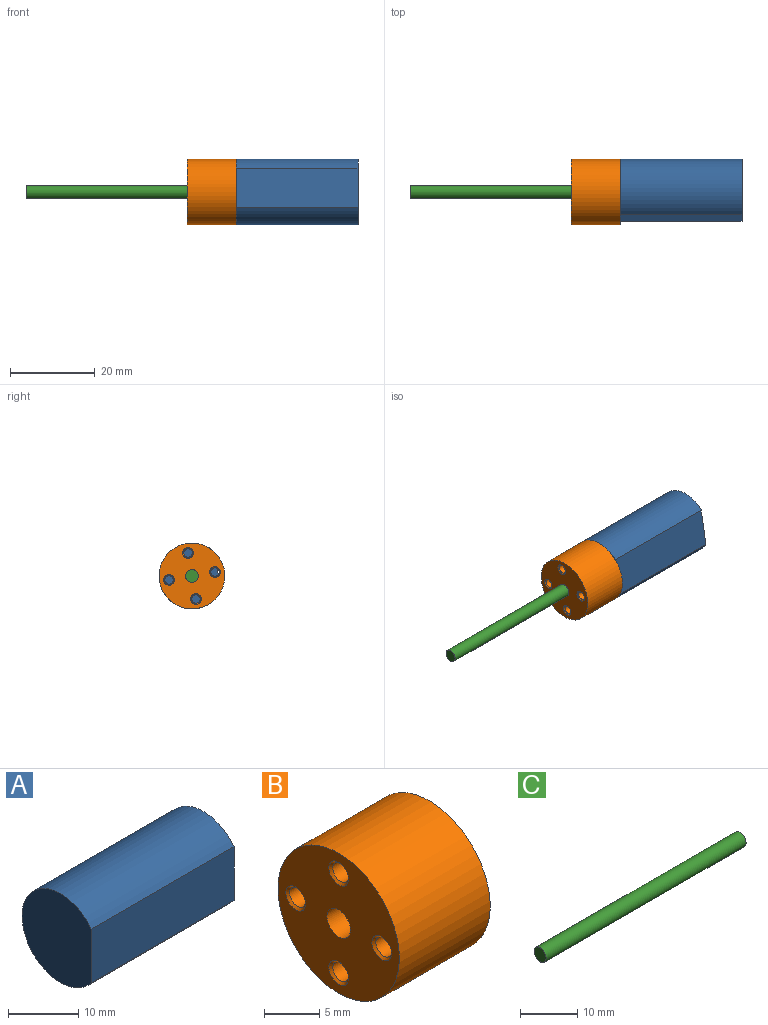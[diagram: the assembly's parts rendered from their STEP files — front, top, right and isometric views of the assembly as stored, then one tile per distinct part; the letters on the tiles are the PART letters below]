
ASSEMBLY  parts=3 mates=2
PART A: 4 faces, bbox 28.7x13.9x15.5 mm
  f0: cylinder r=7.75mm len=28.7mm, axis (-1,0,0), area 1109.8mm2, adj f1,f2,f3
  f1: plane 28.7x9.34mm, normal (0,-1,0), area 268.1mm2, adj f0,f2,f3
  f2: plane 15.5x13.93mm, normal (1,0,0), area 178.7mm2, adj f0,f1
  f3: plane 15.5x13.93mm, normal (-1,0,0), area 178.7mm2, adj f0,f1
PART B: 12 faces, bbox 11.6x15.5x15.5 mm
  f0: cylinder r=1mm len=11.35mm, axis (-1,0,0), area 71.3mm2, adj f6,f11
  f1: cylinder r=1mm len=11.35mm, axis (-1,0,0), area 71.3mm2, adj f6,f9
  f2: cylinder r=1mm len=11.35mm, axis (-1,0,0), area 71.3mm2, adj f6,f8
  f3: cylinder r=1mm len=11.35mm, axis (-1,0,0), area 71.3mm2, adj f6,f10
  f4: cylinder r=1.5mm len=11.6mm, axis (-1,0,0), area 109.3mm2, adj f6,f7
  f5: cylinder r=7.75mm len=15.5mm, axis (-1,0,0), area 564.9mm2, adj f6,f7
  f6: plane 15.5x15.5mm, normal (1,0,0), area 169.1mm2, adj f0,f1,f2,f3,f4,f5
  f7: plane 15.5x15.5mm, normal (-1,0,0), area 162mm2, adj f4,f5,f8,f9,f10,f11
  f8: cone r=1.25mm half-angle=45deg, axis (-1,0,0), area 2.5mm2, adj f2,f7
  f9: cone r=1.25mm half-angle=45deg, axis (-1,0,0), area 2.5mm2, adj f1,f7
  f10: cone r=1.25mm half-angle=45deg, axis (-1,0,0), area 2.5mm2, adj f3,f7
  f11: cone r=1.25mm half-angle=45deg, axis (-1,0,0), area 2.5mm2, adj f0,f7
PART C: 3 faces, bbox 49.6x3x3 mm
  f0: cylinder r=1.5mm len=49.6mm, axis (-1,0,0), area 467.5mm2, adj f1,f2
  f1: plane 3x3mm, normal (1,0,0), area 7.1mm2, adj f0
  f2: plane 3x3mm, normal (-1,0,0), area 7.1mm2, adj f0
PLACE A rot(axis=(-1,0,0),9.7deg) t=(-29.33,-34.96,-5.87)mm
PLACE B rot(axis=(1,0,0),80.3deg) t=(-40.93,10.11,115.59)mm
PLACE C rot(axis=(1,0,0),80.3deg) t=(-78.93,3.49,76.67)mm
MATE fastened C.f0 <-> A.f0  axis (-1,0,0) through (-29.33,-63.42,63.79)mm
MATE fastened A.f0 <-> B.f4  axis (-1,0,0) through (-29.33,-63.42,63.79)mm
